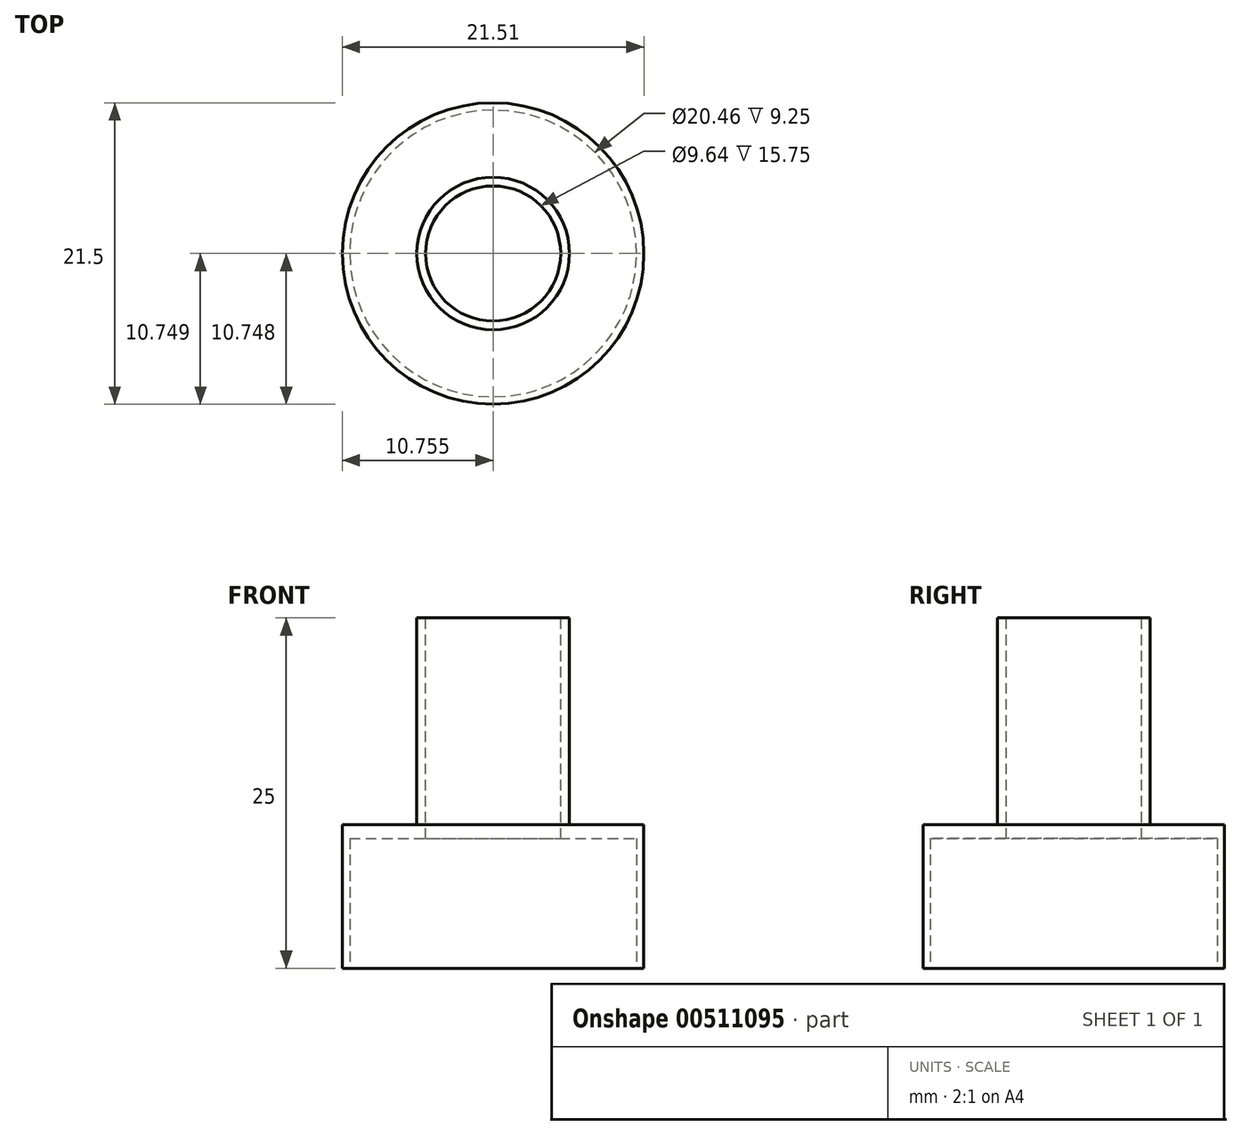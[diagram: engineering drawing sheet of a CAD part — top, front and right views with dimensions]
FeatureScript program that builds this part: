
annotation { "Feature Type Name" : "Feature", "Feature Type Description" : "" }
export const myFeature = defineFeature(function(context is Context, id is Id, definition is map)
    precondition{}
    {
        {
            var Q0;
            Q0=qCreatedBy(makeId("Top.planeOp"),FACE);
            var sketch = newSketch(context, id + "F0", { "sketchPlane" : qUnion([Q0])});
            skCircle(sketch, "E0", {"center": v(24.85, -25.5) * mm, "radius": 10.75 * mm});
            skSolve(sketch);
        }
        {
            var Q0;
            Q0=makeQuery(id+"F0.imprint","IMPRINT",FACE,{"disambiguationData":[TD([[makeQuery(id+"F0.imprint","IMPRINT",EDGE,{"derivedFrom":sQuery(id+"F0.wireOp",EDGE,"E0")}),1.0]])]});
            var sketch = newSketch(context, id + "F1", { "sketchPlane" : qUnion([Q0])});
            skCircle(sketch, "E1", {"center": v(24.85, -25.5) * mm, "radius": 5.44 * mm});
            skSolve(sketch);
        }
        {
            var Q0;
            Q0=makeQuery(id+"F1.imprint","IMPRINT",FACE,{"disambiguationData":[TD([[makeQuery(id+"F1.imprint","IMPRINT",EDGE,{"derivedFrom":sQuery(id+"F1.wireOp",EDGE,"E1")}),1.0]])]});
            extrude(context, id + "F2", {"entities" : qUnion([Q0]), "depth" : 25 * mm});
        }
        {
            var Q0;
            Q0=makeQuery(id+"F0.imprint","IMPRINT",FACE,{"disambiguationData":[TD([[makeQuery(id+"F0.imprint","IMPRINT",EDGE,{"derivedFrom":sQuery(id+"F0.wireOp",EDGE,"E0")}),1.0]])]});
            extrude(context, id + "F3", {"entities" : qUnion([Q0]), "operationType" : NewBodyOperationType.ADD, "depth" : 10.25 * mm});
        }
        {
            var Q0;
            Q0=makeQuery(id+"F3.boolean.opBoolean","MERGE",FACE,{"derivedFrom":[makeQuery(id+"F2.opExtrude","CAP_FACE",FACE,{"disambiguationData":[OSD([sQuery(id+"F1.wireOp",EDGE,"E1")])],"isStart":true}),makeQuery(id+"F3.opExtrude","CAP_FACE",FACE,{"disambiguationData":[OSD([sQuery(id+"F0.wireOp",EDGE,"E0")])],"isStart":true})]});
            var sketch = newSketch(context, id + "F4", { "sketchPlane" : qUnion([Q0])});
            skCircle(sketch, "E2", {"center": v(24.85, 25.5) * mm, "radius": 9.99 * mm});
            skSolve(sketch);
        }
        {
            var Q0;
            Q0=makeQuery(id+"F4.imprint","IMPRINT",FACE,{"disambiguationData":[TD([[makeQuery(id+"F4.imprint","IMPRINT",EDGE,{"derivedFrom":sQuery(id+"F4.wireOp",EDGE,"E2")}),1.0]])]});
            extrude(context, id + "F5", {"entities" : qUnion([Q0]), "operationType" : NewBodyOperationType.ADD, "oppositeDirection" : true, "depth" : 9.25 * mm});
        }
        {
            var Q0;
            Q0=makeQuery(id+"F3.boolean.opBoolean","MERGE",FACE,{"derivedFrom":[makeQuery(id+"F2.opExtrude","CAP_FACE",FACE,{"disambiguationData":[OSD([sQuery(id+"F1.wireOp",EDGE,"E1")])],"isStart":true}),makeQuery(id+"F3.opExtrude","CAP_FACE",FACE,{"disambiguationData":[OSD([sQuery(id+"F0.wireOp",EDGE,"E0")])],"isStart":true})]});
            var sketch = newSketch(context, id + "F6", { "sketchPlane" : qUnion([Q0])});
            skCircle(sketch, "E3", {"center": v(24.85, 25.5) * mm, "radius": 10.12 * mm});
            skSolve(sketch);
        }
        {
            var Q0;
            Q0=makeQuery(id+"F6.imprint","IMPRINT",FACE,{"disambiguationData":[TD([[makeQuery(id+"F6.imprint","IMPRINT",EDGE,{"derivedFrom":sQuery(id+"F6.wireOp",EDGE,"E3")}),1.0]])]});
            extrude(context, id + "F7", {"entities" : qUnion([Q0]), "operationType" : NewBodyOperationType.ADD, "oppositeDirection" : true, "depth" : 9.25 * mm});
        }
        {
            var Q0;
            Q0=makeQuery(id+"F3.boolean.opBoolean","MERGE",FACE,{"derivedFrom":[makeQuery(id+"F2.opExtrude","CAP_FACE",FACE,{"disambiguationData":[OSD([sQuery(id+"F1.wireOp",EDGE,"E1")])],"isStart":true}),makeQuery(id+"F3.opExtrude","CAP_FACE",FACE,{"disambiguationData":[OSD([sQuery(id+"F0.wireOp",EDGE,"E0")])],"isStart":true})]});
            var sketch = newSketch(context, id + "F8", { "sketchPlane" : qUnion([Q0])});
            skCircle(sketch, "E4", {"center": v(24.85, 25.5) * mm, "radius": 10.23 * mm});
            skSolve(sketch);
        }
        {
            var Q0;
            Q0=makeQuery(id+"F8.imprint","IMPRINT",FACE,{"disambiguationData":[TD([[makeQuery(id+"F8.imprint","IMPRINT",EDGE,{"derivedFrom":sQuery(id+"F8.wireOp",EDGE,"E4")}),1.0]])]});
            extrude(context, id + "F9", {"entities" : qUnion([Q0]), "operationType" : NewBodyOperationType.REMOVE, "oppositeDirection" : true, "depth" : 9.25 * mm});
        }
        {
            var Q0;
            Q0=makeQuery(id+"F2.opExtrude","CAP_FACE",FACE,{"disambiguationData":[OSD([sQuery(id+"F1.wireOp",EDGE,"E1")])],"isStart":false});
            var sketch = newSketch(context, id + "F10", { "sketchPlane" : qUnion([Q0])});
            skCircle(sketch, "E5", {"center": v(24.85, -25.5) * mm, "radius": 4.82 * mm});
            skSolve(sketch);
        }
        {
            var Q0;
            Q0=makeQuery(id+"F10.imprint","IMPRINT",FACE,{"disambiguationData":[TD([[makeQuery(id+"F10.imprint","IMPRINT",EDGE,{"derivedFrom":sQuery(id+"F10.wireOp",EDGE,"E5")}),1.0]])]});
            extrude(context, id + "F11", {"entities" : qUnion([Q0]), "operationType" : NewBodyOperationType.REMOVE, "oppositeDirection" : true, "depth" : 25 * mm});
        }
    });
